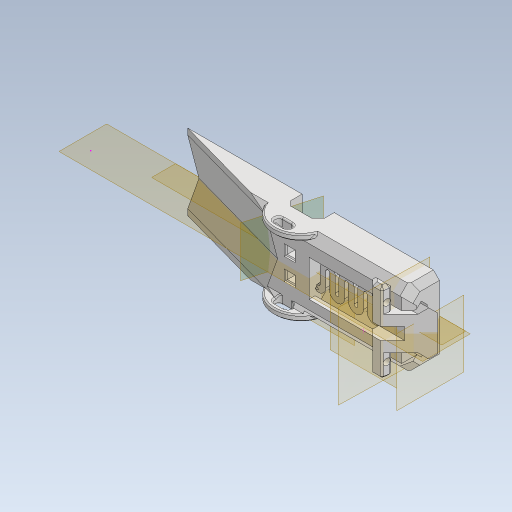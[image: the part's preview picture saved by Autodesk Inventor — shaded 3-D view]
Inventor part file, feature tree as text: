
AUTODESK INVENTOR PART (.ipt)
format: ipt  version: 2023 (Build 270158030, 158C)  size: 771,072 bytes
history: native  units: mm
features: extrude x16, sketch x15, chamfer x13, reference x8, plane x7, other x6, fillet x6, projected_geometry x6, mirror x2
ambient origin geometry x8: Origin, YZ Plane, XZ Plane, XY Plane, X Axis, Y Axis, Z Axis, Center Point
bodies: Body1 (feature_tree), Body2 (feature_tree)
feature tree (79):
  other  "ramp"
  extrude  "Extrusion1"  Depth=10.0mm
  extrude  "Extrusion2"  Depth=10.0mm
  chamfer  "Chamfer2"  Distance=25.0mm
  plane  "Work Plane3"
  extrude  "Extrusion4"  Depth=2.0mm TaperAngle=45.0deg
  chamfer  "Chamfer4"  Distance=1.5mm Angle=45.0deg
  plane  "Work Plane4"
  chamfer  "Chamfer15"  Distance=33.0mm
  sketch  "Sketch5"  dims[d11=33.0mm d12=0.0mm d21=2.0mm d22=2.0mm d23=45.0deg]
  extrude  "Extrusion18"  TaperAngle=90.0deg  [1 undecoded]
  chamfer  "Chamfer16"  [1 undecoded]
  extrude  "Extrusion19"  Depth=3.0mm
  fillet  "Fillet3"  [1 undecoded]
  fillet  "Fillet4"  Radius=2.0mm
  plane  "Work Plane5"
  extrude  "Extrusion20"  Depth=4.0mm
  fillet  "Fillet5"  Radius=4.0mm
  fillet  "Fillet6"  [1 undecoded]
  extrude  "Extrusion8"  Depth=2.0mm
  extrude  "Extrusion9"  Depth=2.0mm
  plane  "Work Plane1"
  extrude  "Extrusion10"  Depth=0.5mm
  extrude  "Extrusion11"  Depth=0.3mm
  extrude  "Extrusion21"  Depth=0.5mm
  chamfer  "Chamfer18"  Distance=5.5mm Angle=45.0deg
  extrude  "Extrusion12"  Depth=0.5mm
  plane  "Work Plane2"
  mirror  "Mirror1"
  chamfer  "Chamfer8"  Distance=4.0mm
  chamfer  "Chamfer19"  Distance=2.5mm
  extrude  "Extrusion22"  Depth=0.5mm TaperAngle=45.0deg
  chamfer  "Chamfer20"  Distance=2.5mm
  chamfer  "Chamfer21"  Distance=3.1mm
  chamfer  "Chamfer22"  Distance=3.1mm
  extrude  "Extrusion23"  Depth=0.5mm
  chamfer  "Chamfer23"  Distance=3.1mm
  chamfer  "Chamfer24"  Distance=3.1mm
  plane  "Work Plane6"
  extrude  "Extrusion24"  Depth=0.5mm
  chamfer  "Chamfer25"  Distance=2.0mm
  extrude  "Extrusion25"  Depth=0.5mm
  fillet  "Fillet7"  Radius=1.2mm
  plane  "Work Plane7"
  mirror  "Mirror2"
  fillet  "Fillet8"  Radius=3.0mm
  reference  "Reference1"
  reference  "Reference2"
  reference  "Reference3"
  reference  "Reference4"
  reference  "Reference5"
  reference  "Reference6"
  sketch  "Sketch2"  dims[d0=10.0mm d1=35.0mm]
  projected_geometry  "Projected Loop1"
  sketch  "Sketch4"  dims[d2=15.0mm d3=10.0mm d4=25.0mm d5=0.0mm]
  projected_geometry  "Projected Loop3"
  sketch  "Sketch9"  dims[d27=4.0mm d28=10.0mm d29=0.0mm d30=0.0mm d34=1.5mm d35=2.0mm d36=45.0deg d74=33.0mm d75=0.0mm]
  sketch  "Sketch10"  dims[d77=0.0mm d78=0.0mm d79=90.0deg]
  sketch  "Sketch11"  dims[d80=1.0mm]
  sketch  "Sketch12"  dims[d81=10.5mm]
  projected_geometry  "Projected Loop4"
  other  "slide"
  reference  "Reference17"
  sketch  "Sketch20"  dims[d82=10.5mm d83=0.0mm d84=0.0mm]
  sketch  "Sketch21"  dims[d86=3.0mm d89=3.0mm d91=0.0mm d92=0.0mm d96=2.0mm d97=0.0mm]
  sketch  "Sketch23"  dims[d98=0.4mm d99=2.0mm d100=45.0deg d144=4.0mm d145=4.0mm d146=45.0deg]
  projected_geometry  "Projected Loop8"
  reference  "Reference18"
  sketch  "Sketch24"  dims[d147=45.0deg d149=2.0mm]
  projected_geometry  "Projected Loop9"
  sketch  "Sketch25"  dims[d150=2.0mm d151=2.0mm]
  sketch  "Sketch27"  dims[d152=0.5mm d153=0.3mm]
  projected_geometry  "Projected Loop10"
  sketch  "Sketch28"  dims[d154=0.3mm d155=0.3mm]
  sketch  "Sketch29"  dims[d156=0.3mm d157=0.5mm d158=5.5mm d159=2.0mm d160=45.0deg d161=4.0mm d162=4.0mm d163=2.5mm d164=0.0mm d165=1.0mm d166=2.0mm d167=45.0deg d176=2.5mm d177=3.1mm d178=3.1mm d179=3.1mm d180=3.1mm d181=3.1mm d182=3.1mm d187=2.0mm d188=2.0mm d190=1.2mm d191=1.2mm d192=3.0mm d193=0.0mm d194=0.6mm d195=2.5mm d196=1.0mm d197=2.0mm d198=1.15mm d199=0.1mm d200=2.4mm d201=0.0mm d205=1.0mm d206=0.5mm d207=1.8mm d208=0.3mm d209=0.3mm d210=0.5mm d211=0.0mm d212=0.3mm d213=2.0mm d214=45.0deg d215=9.0mm d217=5.0mm d218=1.0mm d219=2.0mm d220=45.0deg d221=3.5mm d222=3.5mm d223=4.0mm d224=0.0mm d225=4.0mm d226=2.0mm d227=45.0deg d228=2.0mm d229=2.0mm d230=45.0deg d231=2.5mm d232=2.0mm d233=45.0deg d238=0.5mm d239=7.75mm d240=0.0mm d241=2.5mm d242=2.0mm d243=45.0deg d244=1.0mm d245=2.0mm d246=45.0deg d247=2.1mm d248=3.0mm d249=1.0mm d250=-1.745329mm d251=0.0mm d252=0.0mm d253=1.0mm d254=2.0mm d255=45.0deg d256=2.5mm d257=3.0mm d258=6.5mm d259=0.0mm d260=0.0mm d261=0.5mm d263=1.35mm d264=1.15mm d266=1.2mm d267=1.9mm d268=0.5mm]
  other  "<userpath>\Documents\0004-inventor\3D-CAD-main\trebuchet\V4.0-trebuchet-assembled.iam"
  other  "V4.0-trebuchet-assembled.iam"
  other  "V4-baseplate:1"
  other  "V4-throw-arm:1"
note: 4 required parameter values undecoded (feature->parameter linkage not recoverable at this tier; creation-order binding heuristic only, values carry confidence <= 0.55)
